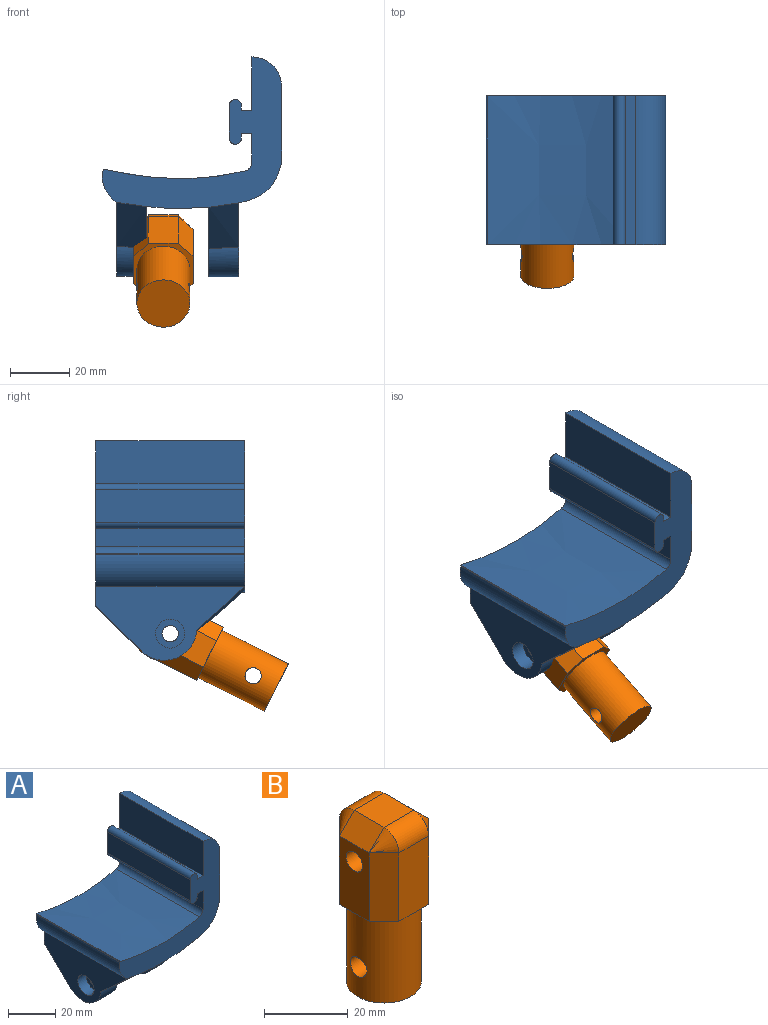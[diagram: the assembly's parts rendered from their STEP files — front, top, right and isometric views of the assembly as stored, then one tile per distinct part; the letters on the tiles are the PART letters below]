
ASSEMBLY  parts=2 mates=1
PART A: 38 faces, bbox 60.3x50x74 mm
  f0: cylinder r=2.75mm len=5.5mm, axis (1,0,0), area 86.4mm2, adj f2,f34
  f1: plane 49.97x24.94mm, normal (-1,0,0), area 691.8mm2, adj f22,f26,f30,f33,f35,f37
  f2: plane 49.82x23.48mm, normal (1,0,0), area 684.7mm2, adj f0,f16,f22,f30,f33,f37
  f3: plane 49.82x23.48mm, normal (-1,0,0), area 684.7mm2, adj f16,f22,f23,f31,f32,f36
  f4: plane 49.97x24.94mm, normal (1,0,0), area 691.8mm2, adj f17,f22,f25,f31,f32,f36
  f5: plane 60.27x50.99mm, normal (0,-1,0), area 1001.1mm2, adj f6,f7,f8,f9,f10,f11,f12,f13
  f6: plane 50x1.6mm, normal (1,0,0), area 80mm2, adj f5,f7,f21,f22
  f7: cylinder r=2.05mm len=50mm, axis (0,1,0), area 322mm2, adj f5,f6,f8,f22
  f8: plane 50x10.9mm, normal (-1,0,0), area 545mm2, adj f5,f7,f9,f22
  f9: cylinder r=2.05mm len=50mm, axis (0,1,0), area 322mm2, adj f5,f8,f10,f22
  f10: plane 50x1.6mm, normal (1,0,0), area 80mm2, adj f5,f9,f11,f22
  f11: plane 50x3.5mm, normal (0,0,-1), area 175mm2, adj f5,f10,f12,f22
  f12: plane 50x9.72mm, normal (-1,0,0), area 485.9mm2, adj f5,f11,f13,f22
  f13: cylinder r=3mm len=50mm, axis (0,1,0), area 197.4mm2, adj f5,f12,f14,f22
  f14: extruded ~50x47.68mm, area 2408.4mm2, adj f5,f13,f15,f22
  f15: plane 50x0.34mm, normal (-0.97,0,0.23), area 17.5mm2, adj f5,f14,f22,f26
  f16: extruded ~50x21mm, area 1051.7mm2, adj f2,f3,f5,f22,f28,f29
  f17: extruded ~50x3.61mm, area 185.2mm2, adj f4,f5,f18,f22,f28
  f18: extruded ~50x12.58mm, area 872mm2, adj f5,f17,f19,f22
  f19: plane 50x25.7mm, normal (1,0,0), area 1284.9mm2, adj f5,f18,f22,f27
  f20: plane 50x18mm, normal (-1,0,0), area 900mm2, adj f5,f21,f22,f27
  f21: plane 50x3.5mm, normal (0,0,1), area 175mm2, adj f5,f6,f20,f22
  f22: plane 60.27x55.55mm, normal (0,1,0), area 1115.7mm2, adj f1,f2,f3,f4,f6,f7,f8,f9
  f23: cylinder r=2.75mm len=5.5mm, axis (1,0,0), area 86.4mm2, adj f3,f24
  f24: plane 9.75x9.75mm, normal (1,0,0), area 50.9mm2, adj f23,f25
  f25: cylinder r=4.88mm len=9.75mm, axis (1,0,0), area 153.2mm2, adj f4,f24
  f26: cylinder r=10mm len=50mm, axis (0,1,0), area 628.9mm2, adj f1,f5,f15,f22,f29
  f27: cylinder r=10mm len=50mm, axis (0,1,0), area 785.4mm2, adj f5,f19,f20,f22
  f28: plane 10x1.46mm, normal (0.14,0,-0.99), area 1.4mm2, adj f5,f16,f17,f36
  f29: plane 10x1.46mm, normal (-0.14,0,-0.99), area 1.4mm2, adj f5,f16,f26,f37
  f30: plane 15.22x15.22mm, normal (0,0.71,-0.71), area 215.3mm2, adj f1,f2,f22,f33
  f31: plane 15.22x15.22mm, normal (0,0.71,-0.71), area 215.3mm2, adj f3,f4,f22,f32
  f32: cylinder r=11mm len=18.74mm, axis (-1,0,0), area 246.9mm2, adj f3,f4,f31,f36
  f33: cylinder r=11mm len=18.74mm, axis (-1,0,0), area 246.9mm2, adj f1,f2,f30,f37
  f34: plane 9.75x9.75mm, normal (-1,0,0), area 50.9mm2, adj f0,f35
  f35: cylinder r=4.88mm len=9.75mm, axis (-1,0,0), area 153.2mm2, adj f1,f34
  f36: bspline ~16.05x15.86mm, area 215.3mm2, adj f3,f4,f28,f32
  f37: bspline ~16.04x15.42mm, area 215.3mm2, adj f1,f2,f29,f33
PART B: 40 faces, bbox 20x20x50 mm
  f0: cylinder r=2.75mm len=5.5mm, axis (1,0,0), area 86.4mm2, adj f7,f39
  f1: cylinder r=2.75mm len=5.5mm, axis (1,0,0), area 17.3mm2, adj f30,f38
  f2: cylinder r=8.9mm len=25mm, axis (0,0,-1), area 1349.9mm2, adj f3,f9,f13
  f3: plane 17.8x17.8mm, normal (0,0,-1), area 248.8mm2, adj f2
  f4: plane 20x10mm, normal (0,-1,0), area 200mm2, adj f9,f12,f18,f23
  f5: plane 20x10mm, normal (1,0,0), area 176.2mm2, adj f9,f10,f19,f21,f23
  f6: plane 20x10mm, normal (0,1,0), area 200mm2, adj f9,f11,f14,f19
  f7: plane 20x10mm, normal (-1,0,0), area 176.2mm2, adj f0,f9,f14,f16,f18
  f8: plane 10x10mm, normal (0,0,1), area 100mm2, adj f11,f12,f16,f21
  f9: plane 20x20mm, normal (0,0,-1), area 101.2mm2, adj f2,f4,f5,f6,f7,f14,f18,f19
  f10: cylinder r=2.75mm len=5.5mm, axis (1,0,0), area 86.4mm2, adj f5,f31
  f11: cylinder r=5mm len=10mm, axis (1,0,0), area 78.5mm2, adj f6,f8,f15,f20
  f12: cylinder r=5mm len=10mm, axis (-1,0,0), area 78.5mm2, adj f4,f8,f17,f22
  f13: cylinder r=2.75mm len=17.8mm, axis (1,0,0), area 300.1mm2, adj f2
  f14: plane 20x5mm, normal (-0.71,0.71,0), area 141.4mm2, adj f6,f7,f9,f15
  f15: cone r=5mm half-angle=45deg, axis (1,0,0), area 27.8mm2, adj f11,f14,f16
  f16: plane 10x5mm, normal (-0.71,0,0.71), area 70.7mm2, adj f7,f8,f15,f17
  f17: cone r=5mm half-angle=45deg, axis (1,0,0), area 27.8mm2, adj f12,f16,f18
  f18: plane 20x5mm, normal (-0.71,-0.71,0), area 141.4mm2, adj f4,f7,f9,f17
  f19: plane 20x5mm, normal (0.71,0.71,0), area 141.4mm2, adj f5,f6,f9,f20
  f20: cone r=5mm half-angle=45deg, axis (-1,0,0), area 27.8mm2, adj f11,f19,f21
  f21: plane 10x5mm, normal (0.71,0,0.71), area 70.7mm2, adj f5,f8,f20,f22
  f22: cone r=5mm half-angle=45deg, axis (-1,0,0), area 27.8mm2, adj f12,f21,f23
  f23: plane 20x5mm, normal (0.71,-0.71,0), area 141.4mm2, adj f4,f5,f9,f22
  f24: plane 4.5x4.2mm, normal (0,-0.87,0.5), area 21.8mm2, adj f25,f29,f30,f31
  f25: plane 4.5x4.2mm, normal (0,-0.87,-0.5), area 21.8mm2, adj f24,f26,f30,f31
  f26: plane 4.85x4.5mm, normal (0,0,-1), area 21.8mm2, adj f25,f27,f30,f31
  f27: plane 4.5x4.2mm, normal (0,0.87,-0.5), area 21.8mm2, adj f26,f28,f30,f31
  f28: plane 4.5x4.2mm, normal (0,0.87,0.5), area 21.8mm2, adj f27,f29,f30,f31
  f29: plane 4.85x4.5mm, normal (0,0,1), area 21.8mm2, adj f24,f28,f30,f31
  f30: plane 9.7x8.4mm, normal (1,0,0), area 37.3mm2, adj f1,f24,f25,f26,f27,f28,f29
  f31: plane 9.7x8.4mm, normal (-1,0,0), area 37.3mm2, adj f10,f24,f25,f26,f27,f28,f29
  f32: plane 4.5x4.2mm, normal (0,-0.87,0.5), area 21.8mm2, adj f33,f37,f38,f39
  f33: plane 4.5x4.2mm, normal (0,-0.87,-0.5), area 21.8mm2, adj f32,f34,f38,f39
  f34: plane 4.85x4.5mm, normal (0,0,-1), area 21.8mm2, adj f33,f35,f38,f39
  f35: plane 4.5x4.2mm, normal (0,0.87,-0.5), area 21.8mm2, adj f34,f36,f38,f39
  f36: plane 4.5x4.2mm, normal (0,0.87,0.5), area 21.8mm2, adj f35,f37,f38,f39
  f37: plane 4.85x4.5mm, normal (0,0,1), area 21.8mm2, adj f32,f36,f38,f39
  f38: plane 9.7x8.4mm, normal (-1,0,0), area 37.3mm2, adj f1,f32,f33,f34,f35,f36,f37
  f39: plane 9.7x8.4mm, normal (1,0,0), area 37.3mm2, adj f0,f32,f33,f34,f35,f36,f37
PLACE A t=(0,-5.71,1.29)mm fixed
PLACE B rot(axis=(-1,0,0),63.1deg) t=(-24.21,-66.38,-56.78)mm
MATE cylindrical B.f0 <-> A.f0  axis (1,0,0) through (-14.21,-30.71,-38.68)mm
